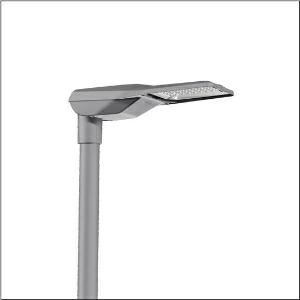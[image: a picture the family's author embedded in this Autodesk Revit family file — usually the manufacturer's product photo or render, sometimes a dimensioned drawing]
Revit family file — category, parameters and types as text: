
# Revit family: streetlight_sl_21_iq_mini___st1_0a_5xe2d61d08hb_7283
name_source: partatom
category: Lighting Fixtures
units: mm (PartAtom-declared; Revit-internal decimal feet)

## family parameters
Cut with Voids When Loaded = No
Host = Face
Light Source = No
Part Type = Normal
Room Calculation Point = No
Round Connector Dimension = Use Diameter
Shared = No

## types (1)
- --- (1 x LED, 8480 lm, 70.9 W, 2700K)
    Apparent Load = 71 VA
    CIE Flux Codes = 37 72 97 100 100
    Color Rendering = 70
    Color Temperature = 2700K
    Default Elevation = 1800 mm
    Description = Streetlight SL 21 iQ mini, mast luminaire, primary light control with lens, of PMMA, primary optical cover: cover, of toughened safety glass, transparent, light distribution: ST1.0a, light emission: direct distribution, primary light characteristic: asymmetric, installation type: post-top, side-entry, LED, High Power LED, rated luminous flux: 8.480lm, luminous efficacy: 120lm/W, light colour: 727, colour temperature: 2700K, control: Auto-Match, Temp-Guard, Lumen-Switch, Night-Set, Smart-Wire, Light-Fading, Desk-Remote (wireless, voltage-free reading and setting of iQ features in the workshop via application-optimized NFC function/RFID function), optimised constant luminous flux control (CLO 2.0), presetting dimming linear, mains connection: 220..240V, AC, 50/60Hz, start of lifetime: 71W, end of service life: 75W, reduction: 31W, luminaire housing, of diecast aluminium, powder-coated, Siteco® metallic grey (DB 702S), corrosivity category C5 mid according to DIN EN ISO 12944, please order mast flange separately, inclination adjustable: 0°, 5°, 10°, 15°, sealing non-destructively replaceable, multi-level sealing system, length: 628mm, width: 235mm, height: 110mm, mast flange for spigot size: 42mm (side-entry): 5XC10008XM4, 60/48mm (side-entry/post-top): 5XC10108XM2, 76/60mm (side-entry/post-top): 5XC10108XM1, protection rating (complete): IP66, insulation class (complete): insulation class II (safety insulation), certification: CE, ENEC, ENEC+, VDE, impact resistance: IK09, permissible operating ambient temperature for outdoor applications: -40..+50°C, standard-compliant lighting for roads and squares, packaging unit: 1 piece

Light Distribution: ST1.0a
    Height = 110 mm
    Lamp = 1 x LED
    Lamp Light Flux = 8480 lm
    Lamp Power = 70.9 W
    Lamp count = 1
    Length = 625 mm
    Luminous efficacy = 120 lm/W
    Manufacturer = Siteco
    ModVariant = No
    Model = 5XE2D61D08HB
    Number of Poles = 1
    OnlyDefault = Yes
    Power Factor = 1
    Product Name = Streetlight SL 21 iQ mini | ST1.0a
    Product group = mast luminaire | pylon top
    ProductGroupID = 6100
    Protection Class = Protection class II
    Protection Degree = IP 66
    RLX_Detail_Level = 1
    RLX_Emergency_Light_Flux = 0 lm
    RLX_Emergency_Type = 0
    RLX_Emergency_Type_DB = No
    RlxData = <blob elided: 91921 chars, md5=baec9383>
    Socket = socket
    Standby Power = 0 W
    System Light Flux = 8480 lm
    System Power = 71 W
    Type Comments = factory setting: luminous flux: 100 % | dim-lin: 254 | 711 mA
    Type Image = l_1003519.jpg
    URL = http://relux.com
    VarID = @adj_090571
    Voltage = 0 V
    Weight = 0.00 kg
    Width = 234 mm

## geometry (parser evidence)
native form markers: Blend x4, Sweep x12
no freeform markers — native parametric forms only
